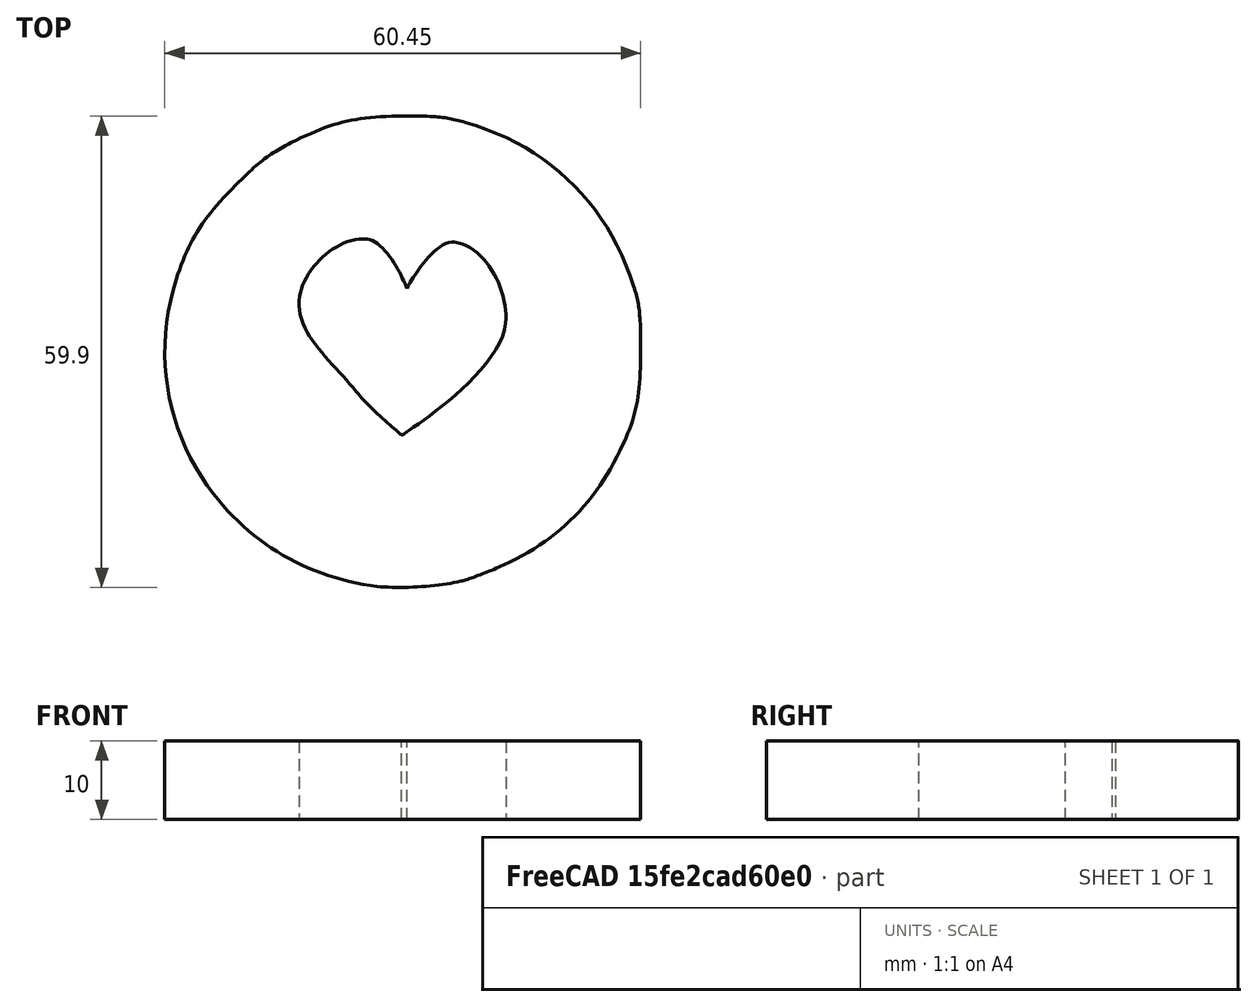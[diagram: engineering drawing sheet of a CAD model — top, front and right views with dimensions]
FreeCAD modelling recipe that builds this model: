
FCSTD DOCUMENT  (FreeCAD 1.0R38806 (Git))
Label: prueba_medallon
License: All rights reserved
LicenseURL: https://en.wikipedia.org/wiki/All_rights_reserved
objects: Part::Extrusion×3, Part::Feature×2, Part::Cut×1
note: 6 computed .brp shape members not serialized (recipe doc carries the construction recipe); baked Part::Feature solids carry a one-line shape summary decoded from their .brp

FEATURE [Part::Feature] path1648
  shape: bbox 62.31 x 60.15 x 2e-07 mm, 1 faces, 0 solids (baked)
FEATURE [Part::Feature] path2953
  Placement = pos=(-52,77,0) rot=(0,0,1;0rad)
  shape: bbox 27.32 x 25.25 x 2e-07 mm, 1 faces, 0 solids (baked)
FEATURE [Part::Extrusion] Extrude
  Base = -> path1648
  Dir = (0,0,1)
  DirMode = 0
  FaceMakerClass = Part::FaceMakerBullseye
  FaceMakerMode = 3
  LengthFwd = 10
  LengthRev = 0
  Solid = false
  Symmetric = false
FEATURE [Part::Extrusion] Extrude001
  Base = -> path1648
  Dir = (0,0,1)
  DirMode = 0
  FaceMakerClass = Part::FaceMakerBullseye
  FaceMakerMode = 3
  LengthFwd = 10
  LengthRev = 0
  Solid = false
  Symmetric = false
FEATURE [Part::Extrusion] Extrude002
  Base = -> path2953
  Dir = (0,0,1)
  DirMode = 0
  FaceMakerClass = Part::FaceMakerBullseye
  FaceMakerMode = 3
  LengthFwd = 10
  LengthRev = 0
  Solid = false
  Symmetric = false
FEATURE [Part::Cut] Cut
  Base = -> Extrude
  Refine = true
  Tool = -> Extrude002
